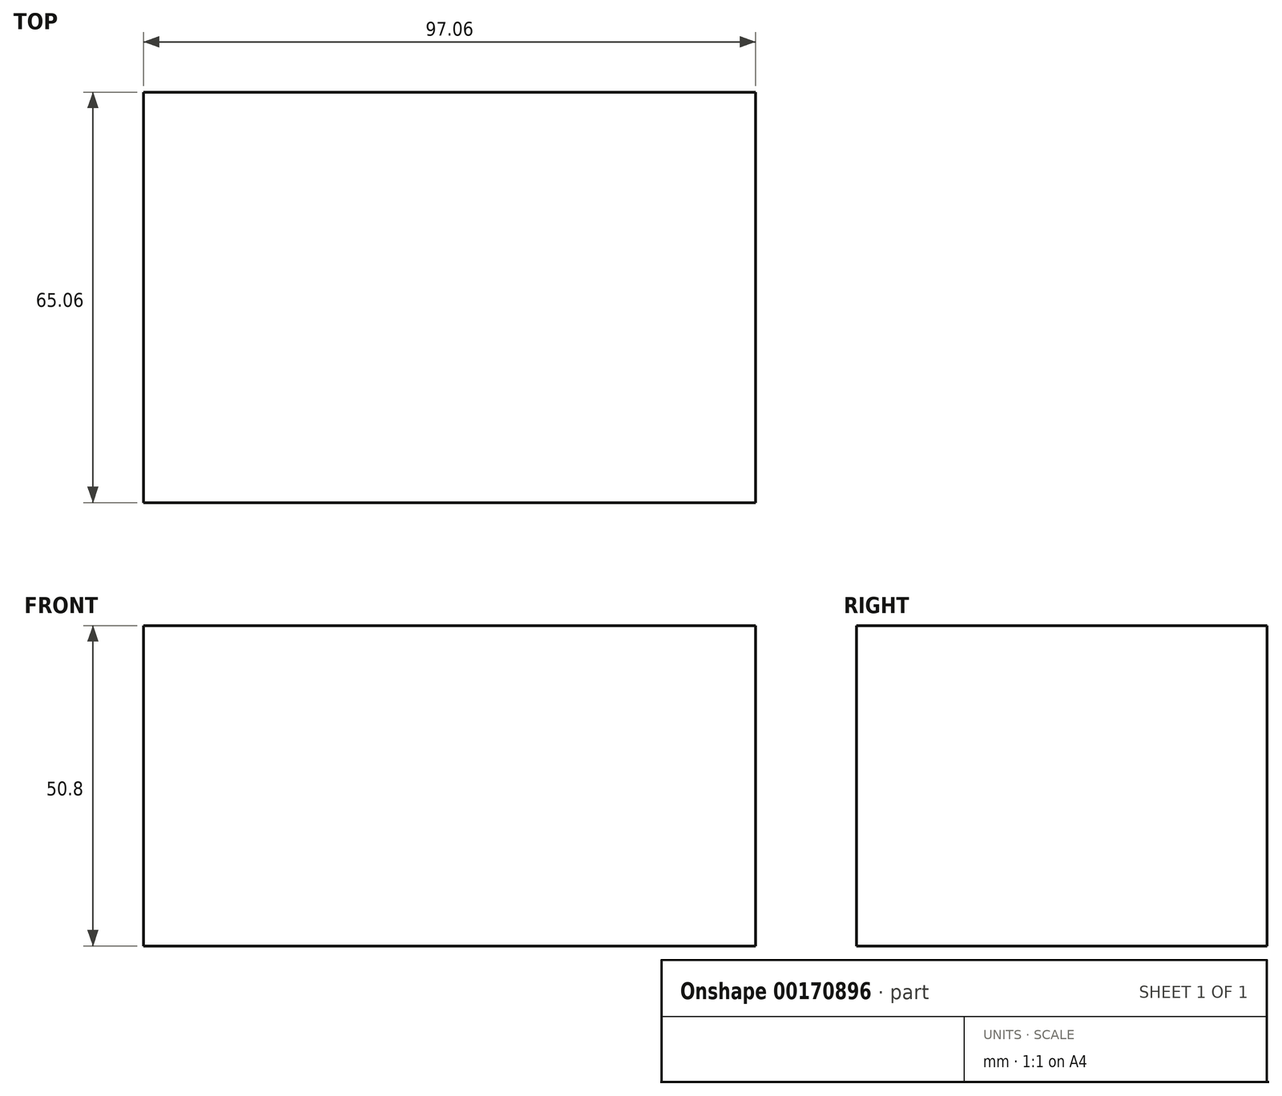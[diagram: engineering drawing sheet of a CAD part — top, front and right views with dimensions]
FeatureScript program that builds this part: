
annotation { "Feature Type Name" : "Feature", "Feature Type Description" : "" }
export const myFeature = defineFeature(function(context is Context, id is Id, definition is map)
    precondition{}
    {
        {
            var Q0;
            Q0=qCreatedBy(makeId("Top.planeOp"),FACE);
            var sketch = newSketch(context, id + "F0", { "sketchPlane" : qUnion([Q0])});
            skLineSegment(sketch, "E0.bottom", {"start": v(-23.23, 29.95) * mm, "end": v(73.83, 29.95) * mm});
            skLineSegment(sketch, "E0.top", {"start": v(-23.23, -35.1) * mm, "end": v(73.83, -35.1) * mm});
            skLineSegment(sketch, "E0.left", {"start": v(-23.23, 29.95) * mm, "end": v(-23.23, -35.1) * mm});
            skLineSegment(sketch, "E0.right", {"start": v(73.83, 29.95) * mm, "end": v(73.83, -35.1) * mm});
            skSolve(sketch);
        }
        {
            var Q0;
            Q0 = qSketchRegion(id + "F0", true);
            extrude(context, id + "F1", {"entities" : qUnion([Q0]), "depth" : 50.8 * mm});
        }
    });
